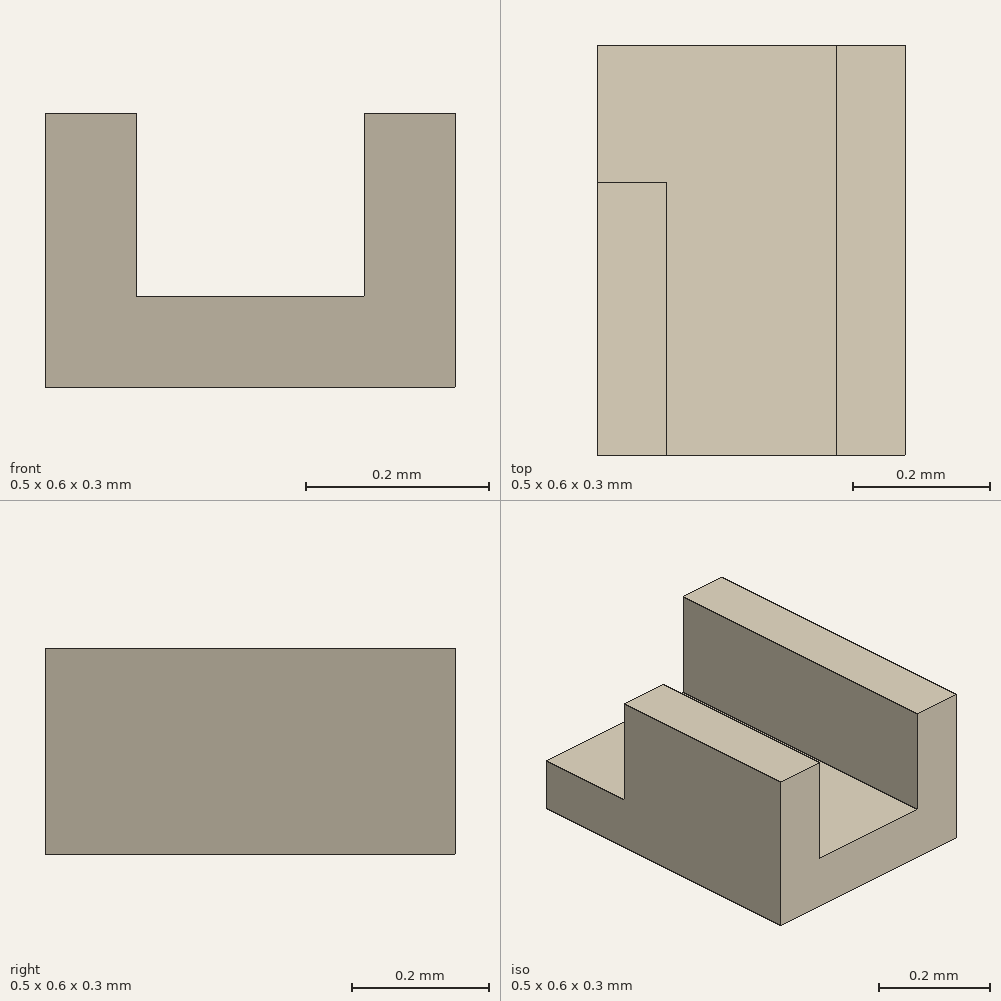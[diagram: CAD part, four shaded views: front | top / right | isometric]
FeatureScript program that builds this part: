
annotation { "Feature Type Name" : "Feature", "Feature Type Description" : "" }
export const myFeature = defineFeature(function(context is Context, id is Id, definition is map)
    precondition{}
    {
        {
            var Q0;
            Q0=qCreatedBy(makeId("Front.planeOp"),FACE);
            var sketch = newSketch(context, id + "F0", { "sketchPlane" : qUnion([Q0])});
            skLineSegment(sketch, "E0.bottom", {"start": v(-0.23, 0.15) * mm, "end": v(-0.13, 0.15) * mm});
            skLineSegment(sketch, "E0.top", {"start": v(-0.23, -0.15) * mm, "end": v(0.22, -0.15) * mm});
            skLineSegment(sketch, "E0.left", {"start": v(-0.23, 0.15) * mm, "end": v(-0.23, -0.15) * mm});
            skLineSegment(sketch, "E0.right", {"start": v(0.23, 0.15) * mm, "end": v(0.23, -0.15) * mm});
            skPoint(sketch, "E0.middle", {"position": v(0, 0) * mm});
            skLineSegment(sketch, "E1", {"start": v(0.12, 0.15) * mm, "end": v(0.12, -0.05) * mm});
            skLineSegment(sketch, "E2.top", {"start": v(0.12, -0.05) * mm, "end": v(-0.13, -0.05) * mm});
            skLineSegment(sketch, "E2.right", {"start": v(-0.13, 0.15) * mm, "end": v(-0.13, -0.05) * mm});
            skLineSegment(sketch, "E3.trimOffspring", {"start": v(0.12, 0.15) * mm, "end": v(0.23, 0.15) * mm});
            skSolve(sketch);
        }
        {
            var Q0;
            Q0 = qSketchRegion(id + "F0", true);
            extrude(context, id + "F1", {"entities" : qUnion([Q0]), "depth" : 0.6 * mm});
        }
        {
            var Q0;
            Q0=makeQuery(id+"F1.opExtrude","SWEPT_FACE",FACE,{"disambiguationData":[OSD([sQuery(id+"F0.wireOp",EDGE,"E0.left")])]});
            var sketch = newSketch(context, id + "F2", { "sketchPlane" : qUnion([Q0])});
            skLineSegment(sketch, "E4.bottom", {"start": v(0, 0.15) * mm, "end": v(0.2, 0.15) * mm});
            skLineSegment(sketch, "E4.top", {"start": v(0, -0.05) * mm, "end": v(0.2, -0.05) * mm});
            skLineSegment(sketch, "E4.left", {"start": v(0, 0.15) * mm, "end": v(0, -0.05) * mm});
            skLineSegment(sketch, "E4.right", {"start": v(0.2, 0.15) * mm, "end": v(0.2, -0.05) * mm});
            skSolve(sketch);
        }
        {
            var Q0;
            Q0=makeQuery(id+"F2.imprint","IMPRINT",FACE,{"disambiguationData":[TD([[makeQuery(id+"F2.imprint","IMPRINT",EDGE,{"derivedFrom":sQuery(id+"F2.wireOp",EDGE,"E4.bottom")}),1.0]])]});
            extrude(context, id + "F3", {"entities" : qUnion([Q0]), "operationType" : NewBodyOperationType.REMOVE, "oppositeDirection" : true, "depth" : 0.2 * mm});
        }
    });
